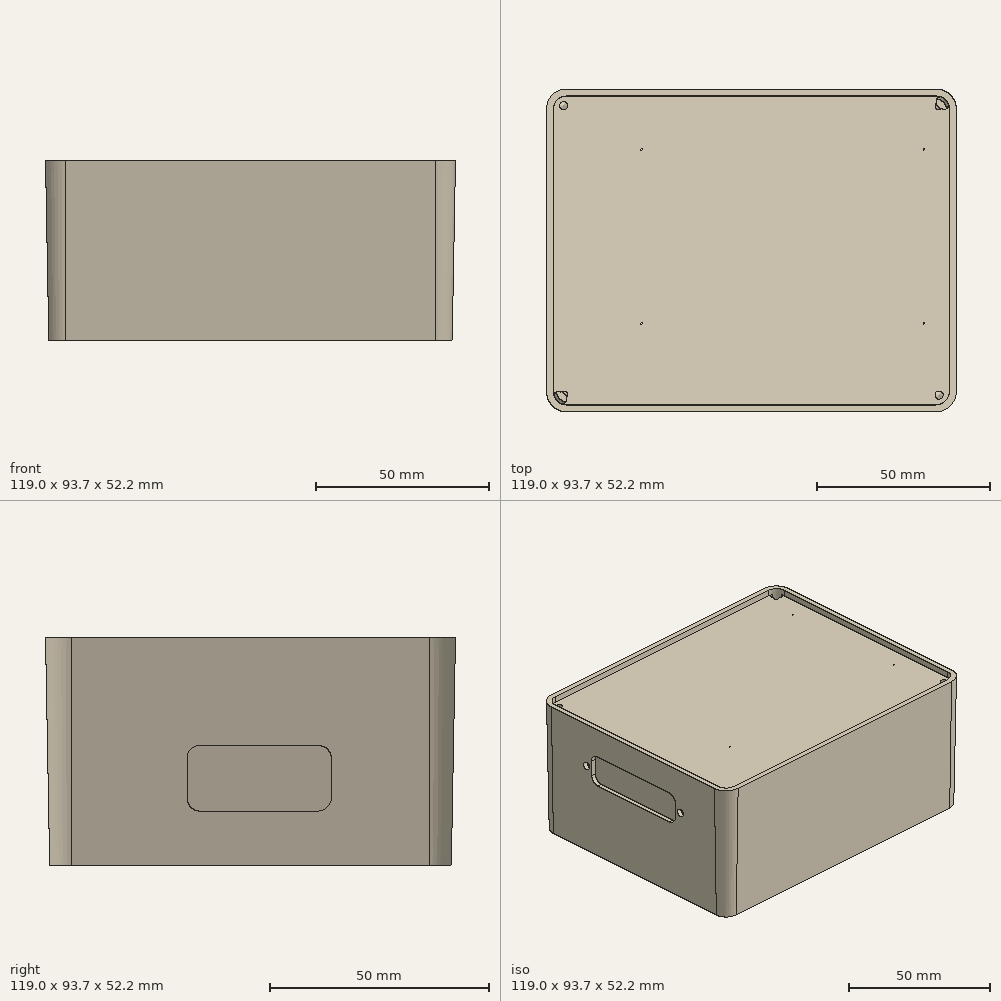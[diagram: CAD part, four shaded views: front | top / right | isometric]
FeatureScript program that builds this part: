
annotation { "Feature Type Name" : "Feature", "Feature Type Description" : "" }
export const myFeature = defineFeature(function(context is Context, id is Id, definition is map)
    precondition{}
    {
        {
            var Q0;
            Q0=qCreatedBy(makeId("Top.planeOp"),FACE);
            var sketch = newSketch(context, id + "F0", { "sketchPlane" : qUnion([Q0])});
            skLineSegment(sketch, "E0.bottom", {"start": v(53.55, 45.9) * mm, "end": v(-53.55, 45.9) * mm});
            skLineSegment(sketch, "E0.top", {"start": v(53.55, -45.9) * mm, "end": v(-53.55, -45.9) * mm});
            skLineSegment(sketch, "E0.left", {"start": v(58.55, 40.9) * mm, "end": v(58.55, -40.9) * mm});
            skLineSegment(sketch, "E0.right", {"start": v(-58.55, 40.9) * mm, "end": v(-58.55, -40.9) * mm});
            skPoint(sketch, "E0.middle", {"position": v(0, 0) * mm});
            skPoint(sketch, "E1.visualSharp", {"position": v(-58.55, 45.9) * mm});
            skArc(sketch, "E1.filletArc", {"start": v(-53.55, 45.9) * mm, "mid": v(-57.09, 44.44) * mm, "end": v(-58.55, 40.9) * mm});
            skPoint(sketch, "E2.visualSharp", {"position": v(-58.55, -45.9) * mm});
            skArc(sketch, "E2.filletArc", {"start": v(-58.55, -40.9) * mm, "mid": v(-57.09, -44.44) * mm, "end": v(-53.55, -45.9) * mm});
            skPoint(sketch, "E3.visualSharp", {"position": v(58.55, -45.9) * mm});
            skArc(sketch, "E3.filletArc", {"start": v(53.55, -45.9) * mm, "mid": v(57.09, -44.44) * mm, "end": v(58.55, -40.9) * mm});
            skPoint(sketch, "E4.visualSharp", {"position": v(58.55, 45.9) * mm});
            skArc(sketch, "E4.filletArc", {"start": v(58.55, 40.9) * mm, "mid": v(57.09, 44.44) * mm, "end": v(53.55, 45.9) * mm});
            skSolve(sketch);
        }
        {
            var Q0;
            Q0=qSketchRegion(id+"F0",true);
            extrude(context, id + "F1", {"entities" : qUnion([Q0]), "depth" : 52.25 * mm, "hasDraft" : true, "draftAngle" : 1.05 * degree});
        }
        {
            var Q0;
            Q0=makeQuery(id+"F1.opExtrude","CAP_FACE",FACE,{"disambiguationData":[OSD([sQuery(id+"F0.wireOp",EDGE,"E0.bottom"),sQuery(id+"F0.wireOp",EDGE,"E0.top"),sQuery(id+"F0.wireOp",EDGE,"E0.left"),sQuery(id+"F0.wireOp",EDGE,"E0.right")])],"isStart":false});
            shell(context, id + "F2", {"entities" : qUnion([Q0]), "thickness" : 2 * mm});
        }
        {
            var Q0;
            Q0=makeQuery(id+"F1.opExtrude","CAP_FACE",FACE,{"disambiguationData":[OSD([sQuery(id+"F0.wireOp",EDGE,"E0.bottom"),sQuery(id+"F0.wireOp",EDGE,"E0.top"),sQuery(id+"F0.wireOp",EDGE,"E0.left"),sQuery(id+"F0.wireOp",EDGE,"E0.right"),sQuery(id+"F0.wireOp",EDGE,"E1.filletArc"),sQuery(id+"F0.wireOp",EDGE,"E2.filletArc"),sQuery(id+"F0.wireOp",EDGE,"E3.filletArc"),sQuery(id+"F0.wireOp",EDGE,"E4.filletArc")])],"isStart":true});
            var sketch = newSketch(context, id + "F3", { "sketchPlane" : qUnion([Q0])});
            skPoint(sketch, "E5", {"position": v(-31.86, 21.25) * mm});
            skPoint(sketch, "E6", {"position": v(50.05, 21.25) * mm});
            skPoint(sketch, "E7", {"position": v(50.05, -29.25) * mm});
            skPoint(sketch, "E8", {"position": v(-31.86, -29.25) * mm});
            skLineSegment(sketch, "E9", {"start": v(-58.55, 0) * mm, "end": v(58.55, 0) * mm, "construction": true});
            skSolve(sketch);
        }
        {
            var Q0;
            Q0=sQuery(id+"F3.wireOp",VERTEX,"E6");
            var Q1;
            Q1=sQuery(id+"F3.wireOp",VERTEX,"E7");
            var Q2;
            Q2=sQuery(id+"F3.wireOp",VERTEX,"E8");
            var Q3;
            Q3=sQuery(id+"F3.wireOp",VERTEX,"E5");
            var Q4;
            Q4=makeQuery(id+"F1.opExtrude","SWEPT_BODY",BODY,{"disambiguationData":[OSD([sQuery(id+"F0.wireOp",EDGE,"E0.bottom"),sQuery(id+"F0.wireOp",EDGE,"E0.top"),sQuery(id+"F0.wireOp",EDGE,"E0.left"),sQuery(id+"F0.wireOp",EDGE,"E0.right"),sQuery(id+"F0.wireOp",EDGE,"E1.filletArc"),sQuery(id+"F0.wireOp",EDGE,"E2.filletArc"),sQuery(id+"F0.wireOp",EDGE,"E3.filletArc"),sQuery(id+"F0.wireOp",EDGE,"E4.filletArc")])]});
            hole(context, id + "F4", {"style" : HoleStyle.C_SINK, "endStyle" : HoleEndStyle.THROUGH, "holeDiameter" : 3 * mm, "cSinkDiameter" : 6.5 * mm, "cSinkAngle" : 90 * degree, "locations" : qUnion([Q0, Q1, Q2, Q3]), "scope" : qUnion([Q4]), "isTappedThrough" : true});
        }
        {
            var Q0;
            Q0=qCreatedBy(makeId("Right.planeOp"),FACE);
            var sketch = newSketch(context, id + "F5", { "sketchPlane" : qUnion([Q0])});
            skLineSegment(sketch, "E10.bottom", {"start": v(15.5, 12.5) * mm, "end": v(-11.5, 12.5) * mm});
            skLineSegment(sketch, "E10.top", {"start": v(15.5, 27.5) * mm, "end": v(-11.5, 27.5) * mm});
            skLineSegment(sketch, "E10.left", {"start": v(18.5, 15.5) * mm, "end": v(18.5, 24.5) * mm});
            skLineSegment(sketch, "E10.right", {"start": v(-14.5, 15.5) * mm, "end": v(-14.5, 24.5) * mm});
            skPoint(sketch, "E10.middle", {"position": v(2, 20) * mm});
            skPoint(sketch, "E11.visualSharp", {"position": v(-14.5, 27.5) * mm});
            skArc(sketch, "E11.filletArc", {"start": v(-11.5, 27.5) * mm, "mid": v(-13.62, 26.62) * mm, "end": v(-14.5, 24.5) * mm});
            skPoint(sketch, "E12.visualSharp", {"position": v(18.5, 27.5) * mm});
            skArc(sketch, "E12.filletArc", {"start": v(18.5, 24.5) * mm, "mid": v(17.62, 26.62) * mm, "end": v(15.5, 27.5) * mm});
            skPoint(sketch, "E13.visualSharp", {"position": v(18.5, 12.5) * mm});
            skArc(sketch, "E13.filletArc", {"start": v(15.5, 12.5) * mm, "mid": v(17.62, 13.38) * mm, "end": v(18.5, 15.5) * mm});
            skPoint(sketch, "E14.visualSharp", {"position": v(-14.5, 12.5) * mm});
            skArc(sketch, "E14.filletArc", {"start": v(-14.5, 15.5) * mm, "mid": v(-13.62, 13.38) * mm, "end": v(-11.5, 12.5) * mm});
            skSolve(sketch);
        }
        {
            var Q0;
            Q0=qSketchRegion(id+"F5",true);
            var Q1;
            Q1=makeQuery(id+"F1.opExtrude","SWEPT_FACE",FACE,{"disambiguationData":[OSD([sQuery(id+"F0.wireOp",EDGE,"E0.left")])]});
            extrude(context, id + "F6", {"entities" : qUnion([Q0]), "operationType" : NewBodyOperationType.REMOVE, "endBound" : BoundingType.UP_TO_SURFACE, "endBoundEntityFace" : qUnion([Q1]), "depth" : 25 * mm});
        }
        {
            var Q0;
            Q0=qCreatedBy(makeId("Right.planeOp"),FACE);
            var sketch = newSketch(context, id + "F7", { "sketchPlane" : qUnion([Q0])});
            skLineSegment(sketch, "E15.bottom", {"start": v(18, 41) * mm, "end": v(-18, 41) * mm});
            skLineSegment(sketch, "E15.top", {"start": v(18, 29) * mm, "end": v(-18, 29) * mm});
            skLineSegment(sketch, "E15.left", {"start": v(21, 38) * mm, "end": v(21, 32) * mm});
            skLineSegment(sketch, "E15.right", {"start": v(-21, 38) * mm, "end": v(-21, 32) * mm});
            skPoint(sketch, "E15.middle", {"position": v(0, 35) * mm});
            skPoint(sketch, "E16.visualSharp", {"position": v(-21, 41) * mm});
            skArc(sketch, "E16.filletArc", {"start": v(-18, 41) * mm, "mid": v(-20.12, 40.12) * mm, "end": v(-21, 38) * mm});
            skPoint(sketch, "E17.visualSharp", {"position": v(-21, 29) * mm});
            skArc(sketch, "E17.filletArc", {"start": v(-21, 32) * mm, "mid": v(-20.12, 29.88) * mm, "end": v(-18, 29) * mm});
            skPoint(sketch, "E18.visualSharp", {"position": v(21, 29) * mm});
            skArc(sketch, "E18.filletArc", {"start": v(18, 29) * mm, "mid": v(20.12, 29.88) * mm, "end": v(21, 32) * mm});
            skPoint(sketch, "E19.visualSharp", {"position": v(21, 41) * mm});
            skArc(sketch, "E19.filletArc", {"start": v(21, 38) * mm, "mid": v(20.12, 40.12) * mm, "end": v(18, 41) * mm});
            skPoint(sketch, "E20", {"position": v(-23.52, 35) * mm});
            skPoint(sketch, "E21", {"position": v(23.52, 35) * mm});
            skLineSegment(sketch, "E22", {"start": v(0, 41) * mm, "end": v(0, 29) * mm, "construction": true});
            skCircle(sketch, "E23", {"center": v(-23.52, 35) * mm, "radius": 1.5 * mm});
            skCircle(sketch, "E24", {"center": v(23.52, 35) * mm, "radius": 1.5 * mm});
            skSolve(sketch);
        }
        {
            var Q0;
            Q0=qSketchRegion(id+"F7",true);
            var Q1;
            Q1=makeQuery(id+"F1.opExtrude","SWEPT_FACE",FACE,{"disambiguationData":[OSD([sQuery(id+"F0.wireOp",EDGE,"E0.right")])]});
            extrude(context, id + "F8", {"entities" : qUnion([Q0]), "operationType" : NewBodyOperationType.REMOVE, "endBound" : BoundingType.UP_TO_SURFACE, "oppositeDirection" : true, "endBoundEntityFace" : qUnion([Q1]), "depth" : 25 * mm});
        }
        {
            var Q0;
            Q0=qCreatedBy(makeId("Front.planeOp"),FACE);
            var sketch = newSketch(context, id + "F9", { "sketchPlane" : qUnion([Q0])});
            skCircle(sketch, "E25", {"center": v(0, 38) * mm, "radius": 4 * mm});
            skPoint(sketch, "E26", {"position": v(30, 38) * mm});
            skCircle(sketch, "E27", {"center": v(30, 38) * mm, "radius": 3.17 * mm});
            skSolve(sketch);
        }
        {
            var Q0;
            Q0=qSketchRegion(id+"F9",true);
            var Q1;
            Q1=makeQuery(id+"F1.opExtrude","SWEPT_FACE",FACE,{"disambiguationData":[OSD([sQuery(id+"F0.wireOp",EDGE,"E0.bottom")])]});
            extrude(context, id + "F10", {"entities" : qUnion([Q0]), "operationType" : NewBodyOperationType.REMOVE, "endBound" : BoundingType.UP_TO_SURFACE, "oppositeDirection" : true, "endBoundEntityFace" : qUnion([Q1]), "depth" : 25 * mm});
        }
        {
            var Q0;
            Q0=makeQuery(id+"F2.opShell","OFFSET_FACE",FACE,{"disambiguationData":[OSD([sQuery(id+"F0.wireOp",EDGE,"E0.bottom"),sQuery(id+"F0.wireOp",EDGE,"E0.top"),sQuery(id+"F0.wireOp",EDGE,"E0.left"),sQuery(id+"F0.wireOp",EDGE,"E0.right"),sQuery(id+"F0.wireOp",EDGE,"E1.filletArc"),sQuery(id+"F0.wireOp",EDGE,"E2.filletArc"),sQuery(id+"F0.wireOp",EDGE,"E3.filletArc"),sQuery(id+"F0.wireOp",EDGE,"E4.filletArc")])]});
            var sketch = newSketch(context, id + "F11", { "sketchPlane" : qUnion([Q0])});
            skLineSegment(sketch, "E28", {"start": v(-56.59, 0) * mm, "end": v(57.5, 0) * mm, "construction": true});
            skPoint(sketch, "E28.endSnap0", {"position": v(56.59, 0) * mm});
            skLineSegment(sketch, "E29", {"start": v(0, 43.94) * mm, "end": v(0, -43.94) * mm, "construction": true});
            skArc(sketch, "E30", {"start": v(-56.59, 39.7) * mm, "mid": v(-53.52, 40.87) * mm, "end": v(-52.36, 43.94) * mm});
            skArc(sketch, "E31.MirrorCS", {"start": v(56.59, 39.7) * mm, "mid": v(53.52, 40.87) * mm, "end": v(52.36, 43.94) * mm});
            skArc(sketch, "E32.MirrorCS", {"start": v(-56.59, -39.7) * mm, "mid": v(-53.52, -40.87) * mm, "end": v(-52.36, -43.94) * mm});
            skArc(sketch, "E33.MirrorCS", {"start": v(56.59, -39.7) * mm, "mid": v(53.52, -40.87) * mm, "end": v(52.36, -43.94) * mm});
            skSolve(sketch);
        }
        {
            var Q0;
            Q0=qSketchRegion(id+"F11",true);
            var Q1;
            {var subQ0=sQuery(id+"F11.wireOp",EDGE,"E30");Q1=makeQuery(id+"F11.imprint","IMPRINT",FACE,{"disambiguationData":[TD([[makeQuery(id+"F11.imprint","IMPRINT",EDGE,{"derivedFrom":subQ0}),1.0]])]});}
            var Q2;
            {var subQ0=sQuery(id+"F11.wireOp",EDGE,"E31.MirrorCS");Q2=makeQuery(id+"F11.imprint","IMPRINT",FACE,{"disambiguationData":[TD([[makeQuery(id+"F11.imprint","IMPRINT",EDGE,{"derivedFrom":subQ0}),-1.0]])]});}
            var Q3;
            {var subQ0=sQuery(id+"F11.wireOp",EDGE,"E33.MirrorCS");Q3=makeQuery(id+"F11.imprint","IMPRINT",FACE,{"disambiguationData":[TD([[makeQuery(id+"F11.imprint","IMPRINT",EDGE,{"derivedFrom":subQ0}),1.0]])]});}
            var Q4;
            {var subQ0=sQuery(id+"F11.wireOp",EDGE,"E32.MirrorCS");Q4=makeQuery(id+"F11.imprint","IMPRINT",FACE,{"disambiguationData":[TD([[makeQuery(id+"F11.imprint","IMPRINT",EDGE,{"derivedFrom":subQ0}),-1.0]])]});}
            extrude(context, id + "F12", {"entities" : qUnion([Q0, Q1, Q2, Q3, Q4]), "operationType" : NewBodyOperationType.ADD, "depth" : 48 * mm, "hasDraft" : true, "draftAngle" : 1.5 * degree});
        }
        {
            var Q0;
            Q0=makeQuery(id+"F12.boolean.opBoolean","INTERSECT",EDGE,{"derivedFrom":[makeQuery(id+"F2.opShell","OFFSET_FACE",FACE,{"disambiguationData":[OSD([sQuery(id+"F0.wireOp",EDGE,"E0.bottom")])]}),makeQuery(id+"F12.opExtrude","SWEPT_FACE",FACE,{"disambiguationData":[OSD([sQuery(id+"F11.wireOp",EDGE,"E31.MirrorCS")])]})]});
            var Q1;
            Q1=makeQuery(id+"F12.boolean.opBoolean","INTERSECT",EDGE,{"derivedFrom":[makeQuery(id+"F2.opShell","OFFSET_FACE",FACE,{"disambiguationData":[OSD([sQuery(id+"F0.wireOp",EDGE,"E0.left")])]}),makeQuery(id+"F12.opExtrude","SWEPT_FACE",FACE,{"disambiguationData":[OSD([sQuery(id+"F11.wireOp",EDGE,"E31.MirrorCS")])]})]});
            var Q2;
            Q2=makeQuery(id+"F12.boolean.opBoolean","INTERSECT",EDGE,{"derivedFrom":[makeQuery(id+"F2.opShell","OFFSET_FACE",FACE,{"disambiguationData":[OSD([sQuery(id+"F0.wireOp",EDGE,"E0.left")])]}),makeQuery(id+"F12.opExtrude","SWEPT_FACE",FACE,{"disambiguationData":[OSD([sQuery(id+"F11.wireOp",EDGE,"E33.MirrorCS")])]})]});
            var Q3;
            Q3=makeQuery(id+"F12.boolean.opBoolean","INTERSECT",EDGE,{"derivedFrom":[makeQuery(id+"F2.opShell","OFFSET_FACE",FACE,{"disambiguationData":[OSD([sQuery(id+"F0.wireOp",EDGE,"E0.top")])]}),makeQuery(id+"F12.opExtrude","SWEPT_FACE",FACE,{"disambiguationData":[OSD([sQuery(id+"F11.wireOp",EDGE,"E33.MirrorCS")])]})]});
            var Q4;
            Q4=makeQuery(id+"F12.boolean.opBoolean","INTERSECT",EDGE,{"derivedFrom":[makeQuery(id+"F2.opShell","OFFSET_FACE",FACE,{"disambiguationData":[OSD([sQuery(id+"F0.wireOp",EDGE,"E0.top")])]}),makeQuery(id+"F12.opExtrude","SWEPT_FACE",FACE,{"disambiguationData":[OSD([sQuery(id+"F11.wireOp",EDGE,"E32.MirrorCS")])]})]});
            var Q5;
            Q5=makeQuery(id+"F12.boolean.opBoolean","INTERSECT",EDGE,{"derivedFrom":[makeQuery(id+"F2.opShell","OFFSET_FACE",FACE,{"disambiguationData":[OSD([sQuery(id+"F0.wireOp",EDGE,"E0.right")])]}),makeQuery(id+"F12.opExtrude","SWEPT_FACE",FACE,{"disambiguationData":[OSD([sQuery(id+"F11.wireOp",EDGE,"E32.MirrorCS")])]})]});
            var Q6;
            Q6=makeQuery(id+"F12.boolean.opBoolean","INTERSECT",EDGE,{"derivedFrom":[makeQuery(id+"F2.opShell","OFFSET_FACE",FACE,{"disambiguationData":[OSD([sQuery(id+"F0.wireOp",EDGE,"E0.right")])]}),makeQuery(id+"F12.opExtrude","SWEPT_FACE",FACE,{"disambiguationData":[OSD([sQuery(id+"F11.wireOp",EDGE,"E30")])]})]});
            var Q7;
            Q7=makeQuery(id+"F12.boolean.opBoolean","INTERSECT",EDGE,{"derivedFrom":[makeQuery(id+"F2.opShell","OFFSET_FACE",FACE,{"disambiguationData":[OSD([sQuery(id+"F0.wireOp",EDGE,"E0.bottom")])]}),makeQuery(id+"F12.opExtrude","SWEPT_FACE",FACE,{"disambiguationData":[OSD([sQuery(id+"F11.wireOp",EDGE,"E30")])]})]});
            fillet(context, id + "F13", {"entities" : qUnion([Q0, Q1, Q2, Q3, Q4, Q5, Q6, Q7]), "radius" : 1 * mm, "tangentPropagation" : true, "allowEdgeOverflow" : false});
        }
        {
            var Q0;
            Q0=makeQuery(id+"F12.opExtrude","CAP_FACE",FACE,{"disambiguationData":[OSD([sQuery(id+"F0.wireOp",EDGE,"E0.bottom"),sQuery(id+"F0.wireOp",EDGE,"E0.right"),sQuery(id+"F0.wireOp",EDGE,"E1.filletArc"),sQuery(id+"F11.wireOp",EDGE,"E30")])],"isStart":false});
            var sketch = newSketch(context, id + "F14", { "sketchPlane" : qUnion([Q0])});
            skPoint(sketch, "E34", {"position": v(-54.5, 42) * mm});
            skPoint(sketch, "E35", {"position": v(54.5, 42) * mm});
            skPoint(sketch, "E36", {"position": v(54.5, -42) * mm});
            skPoint(sketch, "E37", {"position": v(-54.5, -42) * mm});
            skLineSegment(sketch, "E38", {"start": v(-56.24, 0) * mm, "end": v(56.75, 0) * mm, "construction": true});
            skLineSegment(sketch, "E39", {"start": v(0, 43.8) * mm, "end": v(0, -44) * mm, "construction": true});
            skSolve(sketch);
        }
        {
            var Q0;
            Q0=sQuery(id+"F14.wireOp",VERTEX,"E34");
            var Q1;
            Q1=sQuery(id+"F14.wireOp",VERTEX,"E35");
            var Q2;
            Q2=sQuery(id+"F14.wireOp",VERTEX,"E36");
            var Q3;
            Q3=sQuery(id+"F14.wireOp",VERTEX,"E37");
            var Q4;
            Q4=makeQuery(id+"F1.opExtrude","SWEPT_BODY",BODY,{"disambiguationData":[OSD([sQuery(id+"F0.wireOp",EDGE,"E0.bottom"),sQuery(id+"F0.wireOp",EDGE,"E0.top"),sQuery(id+"F0.wireOp",EDGE,"E0.left"),sQuery(id+"F0.wireOp",EDGE,"E0.right"),sQuery(id+"F0.wireOp",EDGE,"E1.filletArc"),sQuery(id+"F0.wireOp",EDGE,"E2.filletArc"),sQuery(id+"F0.wireOp",EDGE,"E3.filletArc"),sQuery(id+"F0.wireOp",EDGE,"E4.filletArc")])]});
            hole(context, id + "F15", {"style" : HoleStyle.SIMPLE, "endStyle" : HoleEndStyle.BLIND, "standardTappedOrClearance" : lookupTablePath({ "standard" : "ISO", "engagement" : "75%", "pitch" : "0.6 mm", "size" : "M3", "type" : "Tapped" }), "standardBlindInLast" : lookupTablePath({ "standard" : "ISO", "engagement" : "75%", "pitch" : "0.6 mm", "size" : "M3", "type" : "Tapped" }), "holeDiameter" : 2.4 * mm, "holeDepth" : 8 * mm, "locations" : qUnion([Q0, Q1, Q2, Q3]), "scope" : qUnion([Q4])});
        }
    });
